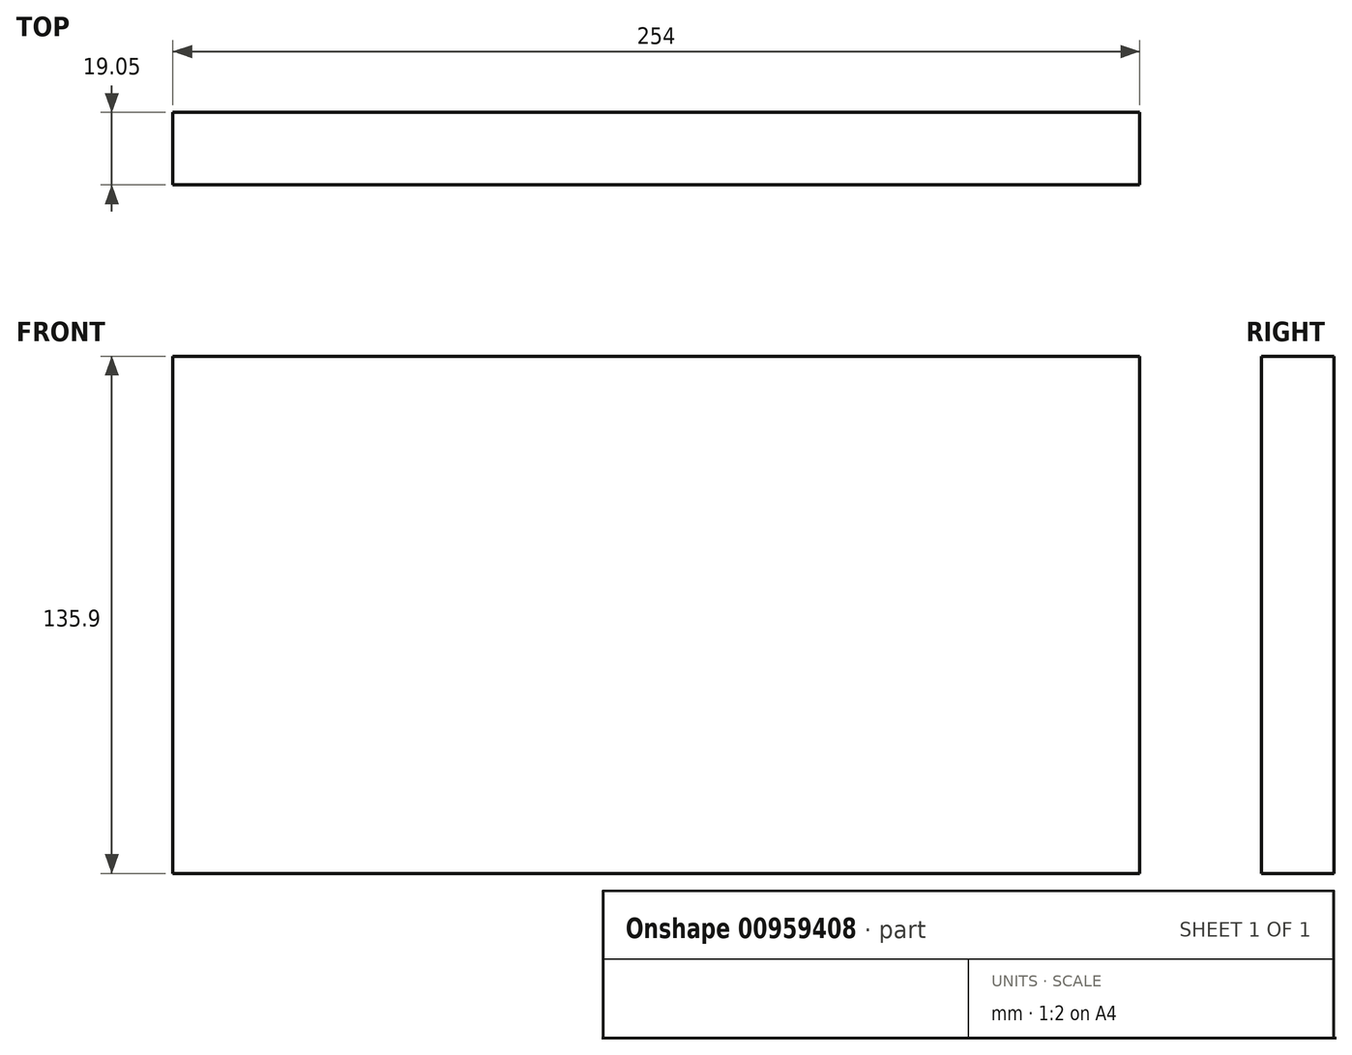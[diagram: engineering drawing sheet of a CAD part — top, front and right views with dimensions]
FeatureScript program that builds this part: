
annotation { "Feature Type Name" : "Feature", "Feature Type Description" : "" }
export const myFeature = defineFeature(function(context is Context, id is Id, definition is map)
    precondition{}
    {
        {
            var Q0;
            Q0=qCreatedBy(makeId("Front.planeOp"),FACE);
            var sketch = newSketch(context, id + "F0", { "sketchPlane" : qUnion([Q0])});
            skLineSegment(sketch, "E0.bottom", {"start": v(127, 67.95) * mm, "end": v(-127, 67.95) * mm});
            skLineSegment(sketch, "E0.top", {"start": v(127, -67.95) * mm, "end": v(-127, -67.95) * mm});
            skLineSegment(sketch, "E0.left", {"start": v(127, 67.95) * mm, "end": v(127, -67.95) * mm});
            skLineSegment(sketch, "E0.right", {"start": v(-127, 67.95) * mm, "end": v(-127, -67.95) * mm});
            skPoint(sketch, "E0.middle", {"position": v(0, 0) * mm});
            skSolve(sketch);
        }
        {
            var Q0;
            Q0=makeQuery(id+"F0.imprint","IMPRINT",FACE,{"disambiguationData":[TD([[makeQuery(id+"F0.imprint","IMPRINT",EDGE,{"derivedFrom":sQuery(id+"F0.wireOp",EDGE,"E0.bottom")}),1.0]])]});
            extrude(context, id + "F1", {"entities" : qUnion([Q0]), "depth" : 19.05 * mm, "offsetDistance" : 25.4 * mm});
        }
    });
